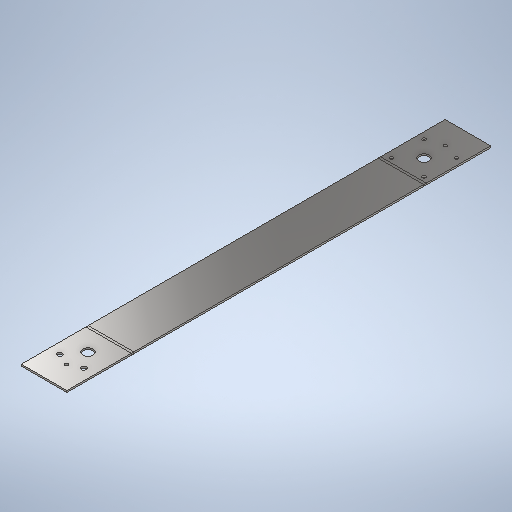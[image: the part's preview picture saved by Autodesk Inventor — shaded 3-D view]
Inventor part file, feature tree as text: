
AUTODESK INVENTOR PART (.ipt)
format: ipt  version: 2025.1 (Build 291241020, 241B)  size: 343,552 bytes
history: native  units: in
note: dims shown in document units (in); Inventor stores cm internally (conversion verified against a paired STEP export)
features: sheet_metal_op x9, sketch x7, hole x4, other x3
ambient origin geometry x8: Origin, YZ Plane, XZ Plane, XY Plane, X Axis, Y Axis, Z Axis, Center Point
bodies: Solid1 (feature_tree)
feature tree (23):
  sheet_metal_op  "Face1"
  sheet_metal_op  "Flange1"
  sheet_metal_op  "Flange2"
  hole  "Hole2"  [1 undecoded]
  hole  "Hole3"  [1 undecoded]
  hole  "Hole4"  [1 undecoded]
  hole  "Hole5"  [1 undecoded]
  sheet_metal_op  "Unfold1"
  sheet_metal_op  "Unfold2"
  sketch  "Sketch2"  dims[d2=1.7in d3=10.875in]
  other  "Plate1"
  sketch  "Sketch3"  dims[d4=0.0625in d5=0.0625in]
  other  "Plate2"
  sheet_metal_op  "Bend1"
  sheet_metal_op  "Corner1"
  sketch  "Sketch4"  dims[d6=0.0312in d7=0.125in]
  other  "Plate3"
  sheet_metal_op  "Bend2"
  sheet_metal_op  "Corner2"
  sketch  "Sketch5"  dims[d8=0.0625in d9=2.5in d10=90.0deg d11=0.03in]
  sketch  "Sketch7"  dims[d12=0.25in]
  sketch  "Sketch8"  dims[d13=0.0625in]
  sketch  "Sketch9"  dims[d14=0.0625in d15=0.0625in d16=0.0312in d17=0.125in d18=0.0625in d19=2.5in d20=90.0deg d21=0.03in d22=0.25in d23=0.0625in d24=0.0625in d37=0.8in d38=0.85in d39=0.85in d40=0.125in d41=0.75in d42=0.375in d43=0.25in d44=0.5635in d45=1.0in d46=0.8108in d47=0.398in d48=0.75in d49=0.375in d50=0.25in d51=0.5635in d52=1.0in d53=0.8108in d54=0.4in d55=0.4in d56=0.6in d57=0.6in d58=0.1875in d59=0.75in d60=0.375in d61=0.25in d62=0.5635in d63=1.0in d64=0.8108in d65=0.61in d68=0.61in d69=0.61in d70=0.61in d71=0.61in d72=0.61in d73=0.61in d74=0.61in d75=0.125in d76=0.75in d77=0.375in d78=0.25in d79=0.5635in d80=1.0in d81=0.8108in d83=0.8in d29=1.0in d30=1.0in d31=1.0in d32=0.15in d33=0.25in d34=0.375in d35=0.5635in d36=0.75in]
note: 4 required parameter values undecoded (feature->parameter linkage not recoverable at this tier; creation-order binding heuristic only, values carry confidence <= 0.55)
